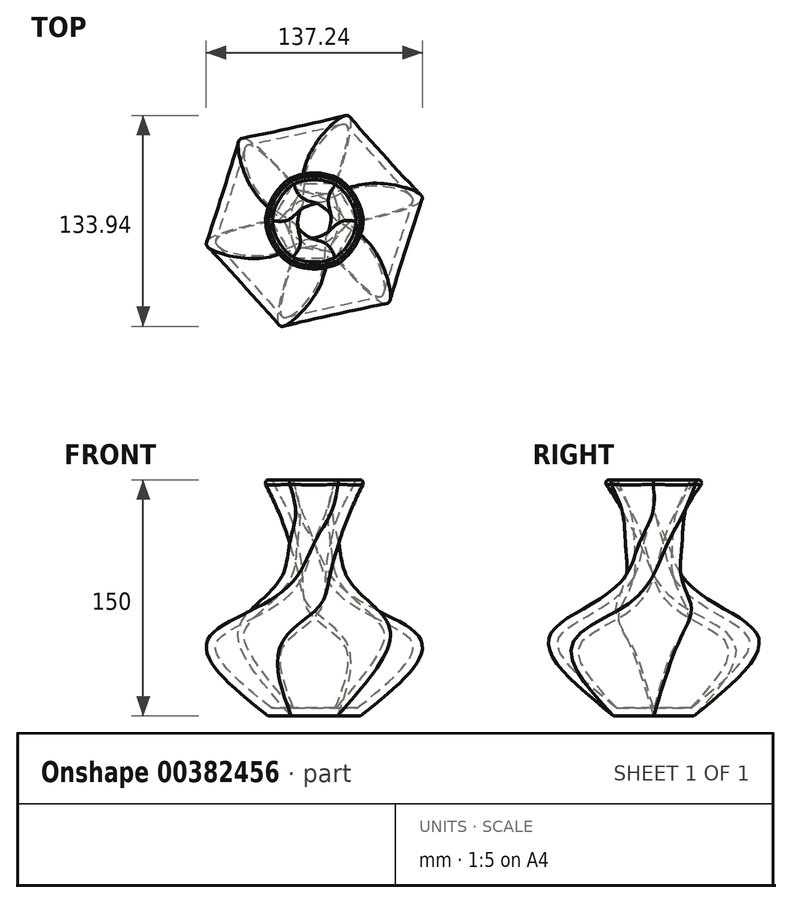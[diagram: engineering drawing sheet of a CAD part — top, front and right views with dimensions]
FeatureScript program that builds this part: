
annotation { "Feature Type Name" : "Feature", "Feature Type Description" : "" }
export const myFeature = defineFeature(function(context is Context, id is Id, definition is map)
    precondition{}
    {
        {
            var Q0;
            Q0=qCreatedBy(makeId("Top.planeOp"),FACE);
            var sketch = newSketch(context, id + "F0", { "sketchPlane" : qUnion([Q0])});
            skCircle(sketch, "E0.cCircle", {"center": v(0, 0) * mm, "radius": 25.51 * mm, "construction": true});
            skLineSegment(sketch, "E0.0", {"start": v(-14.73, -25.51) * mm, "end": v(-29.46, 0) * mm});
            skLineSegment(sketch, "E0.1", {"start": v(-29.46, 0) * mm, "end": v(-14.73, 25.51) * mm});
            skLineSegment(sketch, "E0.2", {"start": v(-14.73, 25.51) * mm, "end": v(14.73, 25.51) * mm});
            skLineSegment(sketch, "E0.3", {"start": v(14.73, 25.51) * mm, "end": v(29.46, 0) * mm});
            skLineSegment(sketch, "E0.4", {"start": v(29.46, 0) * mm, "end": v(14.73, -25.51) * mm});
            skLineSegment(sketch, "E0.5", {"start": v(14.73, -25.51) * mm, "end": v(-14.73, -25.51) * mm});
            skPoint(sketch, "E0.0.midPoint", {"position": v(-22.1, -12.76) * mm});
            skSolve(sketch);
        }
        {
            var Q0;
            Q0=qCreatedBy(makeId("Top.planeOp"),FACE);
            cPlane(context, id + "F1", {"entities" : qUnion([Q0]), "cplaneType" : CPlaneType.OFFSET, "offset" : 50 * mm, "width" : 150 * mm, "height" : 150 * mm});
        }
        {
            var Q0;
            Q0=qCreatedBy(id+"F1.planeOp",FACE);
            var sketch = newSketch(context, id + "F2", { "sketchPlane" : qUnion([Q0])});
            skCircle(sketch, "E1.cCircle", {"center": v(0, 0) * mm, "radius": 59.72 * mm, "construction": true});
            skLineSegment(sketch, "E1.0", {"start": v(-18.44, -66.44) * mm, "end": v(-66.76, -17.25) * mm});
            skLineSegment(sketch, "E1.1", {"start": v(-66.76, -17.25) * mm, "end": v(-48.32, 49.2) * mm});
            skLineSegment(sketch, "E1.2", {"start": v(-48.32, 49.2) * mm, "end": v(18.44, 66.44) * mm});
            skLineSegment(sketch, "E1.3", {"start": v(18.44, 66.44) * mm, "end": v(66.76, 17.25) * mm});
            skLineSegment(sketch, "E1.4", {"start": v(66.76, 17.25) * mm, "end": v(48.32, -49.2) * mm});
            skLineSegment(sketch, "E1.5", {"start": v(48.32, -49.2) * mm, "end": v(-18.44, -66.44) * mm});
            skPoint(sketch, "E1.0.midPoint", {"position": v(-42.6, -41.85) * mm});
            skSolve(sketch);
        }
        {
            var Q0;
            Q0=qCreatedBy(makeId("Top.planeOp"),FACE);
            cPlane(context, id + "F3", {"entities" : qUnion([Q0]), "cplaneType" : CPlaneType.OFFSET, "offset" : 150 * mm, "width" : 150 * mm, "height" : 150 * mm});
        }
        {
            var Q0;
            Q0=qCreatedBy(id+"F3.planeOp",FACE);
            var sketch = newSketch(context, id + "F4", { "sketchPlane" : qUnion([Q0])});
            skCircle(sketch, "E2", {"center": v(0, 0) * mm, "radius": 32.32 * mm});
            skSolve(sketch);
        }
        {
            var Q0;
            Q0=qCreatedBy(makeId("Top.planeOp"),FACE);
            cPlane(context, id + "F5", {"entities" : qUnion([Q0]), "cplaneType" : CPlaneType.OFFSET, "offset" : 70 * mm, "width" : 150 * mm, "height" : 150 * mm});
        }
        {
            var Q0;
            Q0=qCreatedBy(id+"F5.planeOp",FACE);
            var sketch = newSketch(context, id + "F6", { "sketchPlane" : qUnion([Q0])});
            skCircle(sketch, "E3.cCircle", {"center": v(0, 0) * mm, "radius": 36.15 * mm, "construction": true});
            skLineSegment(sketch, "E3.0", {"start": v(37.73, -17.86) * mm, "end": v(3.4, -41.6) * mm});
            skLineSegment(sketch, "E3.1", {"start": v(3.4, -41.6) * mm, "end": v(-34.33, -23.75) * mm});
            skLineSegment(sketch, "E3.2", {"start": v(-34.33, -23.75) * mm, "end": v(-37.73, 17.86) * mm});
            skLineSegment(sketch, "E3.3", {"start": v(-37.73, 17.86) * mm, "end": v(-3.4, 41.6) * mm});
            skLineSegment(sketch, "E3.4", {"start": v(-3.4, 41.6) * mm, "end": v(34.33, 23.75) * mm});
            skLineSegment(sketch, "E3.5", {"start": v(34.33, 23.75) * mm, "end": v(37.73, -17.86) * mm});
            skPoint(sketch, "E3.0.midPoint", {"position": v(20.56, -29.73) * mm});
            skSolve(sketch);
        }
        {
            var Q0;
            Q0=qCreatedBy(makeId("Top.planeOp"),FACE);
            cPlane(context, id + "F7", {"entities" : qUnion([Q0]), "cplaneType" : CPlaneType.OFFSET, "offset" : 90 * mm, "width" : 150 * mm, "height" : 150 * mm});
        }
        {
            var Q0;
            Q0=qCreatedBy(id+"F7.planeOp",FACE);
            var sketch = newSketch(context, id + "F8", { "sketchPlane" : qUnion([Q0])});
            skCircle(sketch, "E4.cCircle", {"center": v(0, 0) * mm, "radius": 17.3 * mm, "construction": true});
            skLineSegment(sketch, "E4.0", {"start": v(19.96, 0) * mm, "end": v(9.98, 17.3) * mm});
            skLineSegment(sketch, "E4.1", {"start": v(9.98, -17.3) * mm, "end": v(19.96, 0) * mm});
            skLineSegment(sketch, "E4.2", {"start": v(-9.98, -17.3) * mm, "end": v(9.98, -17.3) * mm});
            skLineSegment(sketch, "E4.3", {"start": v(-19.96, 0) * mm, "end": v(-9.98, -17.3) * mm});
            skLineSegment(sketch, "E4.4", {"start": v(-9.98, 17.3) * mm, "end": v(-19.96, 0) * mm});
            skLineSegment(sketch, "E4.5", {"start": v(9.98, 17.3) * mm, "end": v(-9.98, 17.3) * mm});
            skPoint(sketch, "E4.0.midPoint", {"position": v(14.97, 8.65) * mm});
            skSolve(sketch);
        }
        {
            var Q0;
            Q0=qCreatedBy(makeId("Top.planeOp"),FACE);
            cPlane(context, id + "F9", {"entities" : qUnion([Q0]), "cplaneType" : CPlaneType.OFFSET, "offset" : 110 * mm, "width" : 150 * mm, "height" : 150 * mm});
        }
        {
            var Q0;
            Q0=qCreatedBy(id+"F9.planeOp",FACE);
            var sketch = newSketch(context, id + "F10", { "sketchPlane" : qUnion([Q0])});
            skCircle(sketch, "E5.cCircle", {"center": v(0, 0) * mm, "radius": 15.58 * mm, "construction": true});
            skLineSegment(sketch, "E5.0", {"start": v(15.58, -9) * mm, "end": v(0, -17.99) * mm});
            skLineSegment(sketch, "E5.1", {"start": v(0, -17.99) * mm, "end": v(-15.58, -9) * mm});
            skLineSegment(sketch, "E5.2", {"start": v(-15.58, -9) * mm, "end": v(-15.58, 9) * mm});
            skLineSegment(sketch, "E5.3", {"start": v(-15.58, 9) * mm, "end": v(0, 17.99) * mm});
            skLineSegment(sketch, "E5.4", {"start": v(0, 17.99) * mm, "end": v(15.58, 9) * mm});
            skLineSegment(sketch, "E5.5", {"start": v(15.58, 9) * mm, "end": v(15.58, -9) * mm});
            skPoint(sketch, "E5.0.midPoint", {"position": v(7.79, -13.5) * mm});
            skSolve(sketch);
        }
        {
            var Q0;
            Q0=qCreatedBy(makeId("Top.planeOp"),FACE);
            cPlane(context, id + "F11", {"entities" : qUnion([Q0]), "cplaneType" : CPlaneType.OFFSET, "offset" : 130 * mm, "width" : 150 * mm, "height" : 150 * mm});
        }
        {
            var Q0;
            Q0=qCreatedBy(id+"F11.planeOp",FACE);
            var sketch = newSketch(context, id + "F12", { "sketchPlane" : qUnion([Q0])});
            skCircle(sketch, "E6.cCircle", {"center": v(0, 0) * mm, "radius": 22.83 * mm, "construction": true});
            skLineSegment(sketch, "E6.0", {"start": v(-22.82, 0.5) * mm, "end": v(-10.98, 20.01) * mm});
            skLineSegment(sketch, "E6.1", {"start": v(-10.98, 20.01) * mm, "end": v(11.84, 19.52) * mm});
            skLineSegment(sketch, "E6.2", {"start": v(11.84, 19.52) * mm, "end": v(22.82, -0.5) * mm});
            skLineSegment(sketch, "E6.3", {"start": v(22.82, -0.5) * mm, "end": v(10.98, -20.01) * mm});
            skLineSegment(sketch, "E6.4", {"start": v(10.98, -20.01) * mm, "end": v(-11.84, -19.52) * mm});
            skLineSegment(sketch, "E6.5", {"start": v(-11.84, -19.52) * mm, "end": v(-22.82, 0.5) * mm});
            skSolve(sketch);
        }
        {
            var Q0;
            Q0=makeQuery(id+"F0.imprint","IMPRINT",FACE,{"disambiguationData":[TD([[makeQuery(id+"F0.imprint","IMPRINT",EDGE,{"derivedFrom":sQuery(id+"F0.wireOp",EDGE,"E0.0")}),-1.0]])]});
            var Q1;
            Q1=makeQuery(id+"F2.imprint","IMPRINT",FACE,{"disambiguationData":[TD([[makeQuery(id+"F2.imprint","IMPRINT",EDGE,{"derivedFrom":sQuery(id+"F2.wireOp",EDGE,"E1.0")}),-1.0]])]});
            var Q2;
            Q2=makeQuery(id+"F6.imprint","IMPRINT",FACE,{"disambiguationData":[TD([[makeQuery(id+"F6.imprint","IMPRINT",EDGE,{"derivedFrom":sQuery(id+"F6.wireOp",EDGE,"E3.0")}),-1.0]])]});
            var Q3;
            Q3 = qSketchRegion(id + "F8", true);
            var Q4;
            Q4 = qSketchRegion(id + "F10", true);
            var Q5;
            Q5 = qSketchRegion(id + "F12", true);
            var Q6;
            Q6=makeQuery(id+"F4.imprint","IMPRINT",FACE,{"disambiguationData":[TD([[makeQuery(id+"F4.imprint","IMPRINT",EDGE,{"derivedFrom":sQuery(id+"F4.wireOp",EDGE,"E2")}),1.0]])]});
            loft(context, id + "F13", {"sheetProfilesArray" : [{ "sheetProfileEntities" : qUnion([Q0]) }, { "sheetProfileEntities" : qUnion([Q1]) }, { "sheetProfileEntities" : qUnion([Q2]) }, { "sheetProfileEntities" : qUnion([Q3]) }, { "sheetProfileEntities" : qUnion([Q4]) }, { "sheetProfileEntities" : qUnion([Q5]) }, { "sheetProfileEntities" : qUnion([Q6]) }]});
        }
        {
            var Q0;
            Q0=makeQuery(id+"F13.opLoft","MID_CAP_EDGE",EDGE,{"disambiguationData":[OSD([sQuery(id+"F0.wireOp",EDGE,"E0.0"),sQuery(id+"F0.wireOp",EDGE,"E0.4"),sQuery(id+"F0.wireOp",EDGE,"E0.5"),sQuery(id+"F4.wireOp",EDGE,"E2")])],"capPos":6.0});
            var Q1;
            Q1=makeQuery(id+"F13.opLoft","MID_CAP_EDGE",EDGE,{"disambiguationData":[OSD([sQuery(id+"F0.wireOp",EDGE,"E0.0"),sQuery(id+"F0.wireOp",EDGE,"E0.5"),sQuery(id+"F4.wireOp",EDGE,"E2"),sQuery(id+"F12.wireOp",EDGE,"E6.2"),sQuery(id+"F12.wireOp",EDGE,"E6.3")])],"capPos":6.0});
            var Q2;
            Q2=makeQuery(id+"F13.opLoft","MID_CAP_EDGE",EDGE,{"disambiguationData":[OSD([sQuery(id+"F0.wireOp",EDGE,"E0.1"),sQuery(id+"F0.wireOp",EDGE,"E0.2"),sQuery(id+"F4.wireOp",EDGE,"E2"),sQuery(id+"F12.wireOp",EDGE,"E6.2"),sQuery(id+"F12.wireOp",EDGE,"E6.3")])],"capPos":6.0});
            var Q3;
            Q3=makeQuery(id+"F13.opLoft","MID_CAP_EDGE",EDGE,{"disambiguationData":[OSD([sQuery(id+"F0.wireOp",EDGE,"E0.1"),sQuery(id+"F0.wireOp",EDGE,"E0.2"),sQuery(id+"F0.wireOp",EDGE,"E0.3"),sQuery(id+"F4.wireOp",EDGE,"E2")])],"capPos":6.0});
            var Q4;
            Q4=makeQuery(id+"F13.opLoft","MID_CAP_EDGE",EDGE,{"disambiguationData":[OSD([sQuery(id+"F0.wireOp",EDGE,"E0.2"),sQuery(id+"F0.wireOp",EDGE,"E0.3"),sQuery(id+"F0.wireOp",EDGE,"E0.4"),sQuery(id+"F4.wireOp",EDGE,"E2")])],"capPos":6.0});
            var Q5;
            Q5=makeQuery(id+"F13.opLoft","MID_CAP_EDGE",EDGE,{"disambiguationData":[OSD([sQuery(id+"F0.wireOp",EDGE,"E0.3"),sQuery(id+"F0.wireOp",EDGE,"E0.4"),sQuery(id+"F0.wireOp",EDGE,"E0.5"),sQuery(id+"F4.wireOp",EDGE,"E2")])],"capPos":6.0});
            fillet(context, id + "F14", {"entities" : qUnion([Q0, Q1, Q2, Q3, Q4, Q5]), "radius" : 2 * mm, "tangentPropagation" : true, "allowEdgeOverflow" : false});
        }
        {
            var Q0;
            Q0=makeQuery(id+"F13.opLoft","CAP_FACE",FACE,{"disambiguationData":[OSD([makeQuery(id+"F4.imprint","IMPRINT",FACE,{"disambiguationData":[TD([[makeQuery(id+"F4.imprint","IMPRINT",EDGE,{"derivedFrom":sQuery(id+"F4.wireOp",EDGE,"E2")}),1.0]])]})])],"isStart":true});
            shell(context, id + "F15", {"entities" : qUnion([Q0]), "thickness" : 5 * mm});
        }
    });
